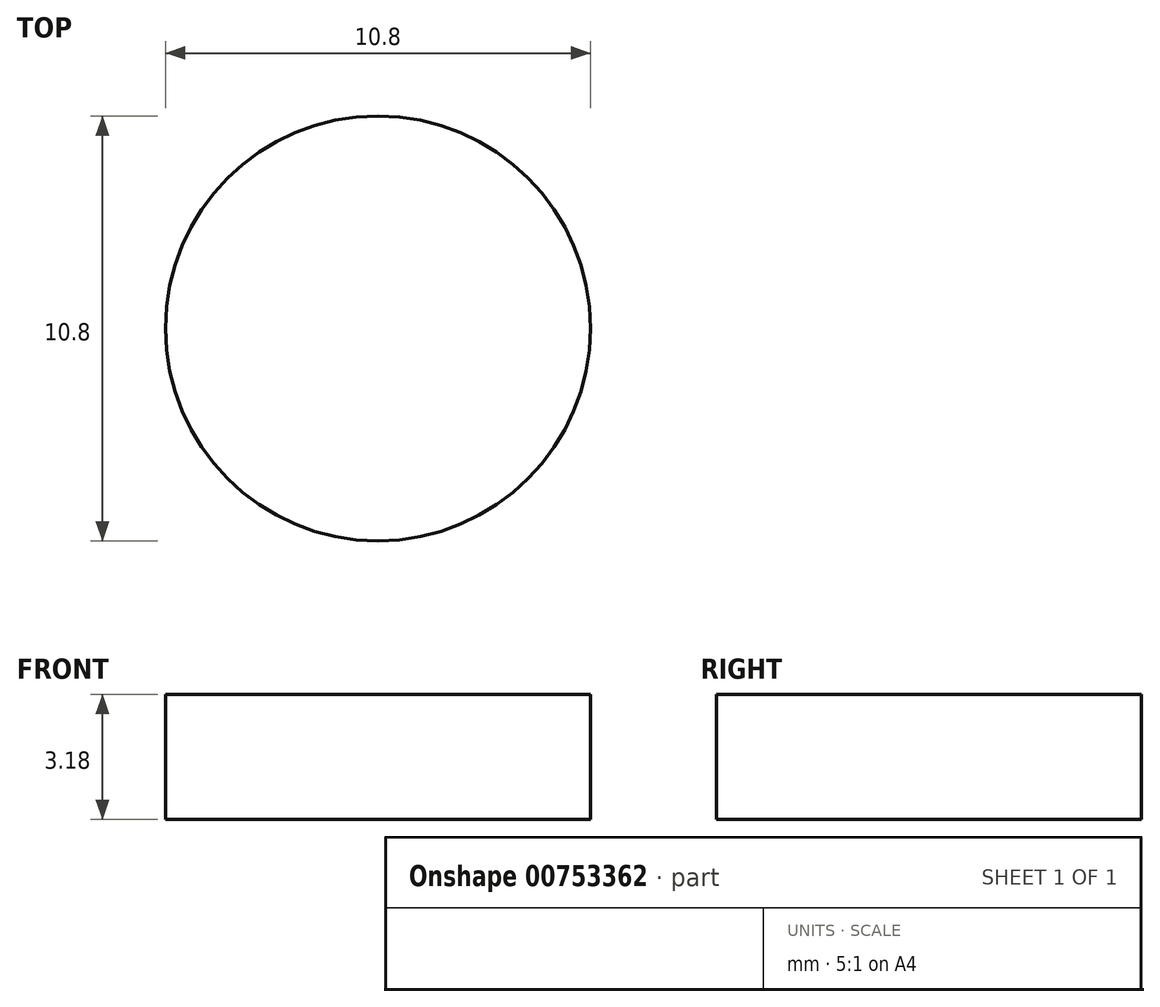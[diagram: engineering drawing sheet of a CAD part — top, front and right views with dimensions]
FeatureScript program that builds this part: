
annotation { "Feature Type Name" : "Feature", "Feature Type Description" : "" }
export const myFeature = defineFeature(function(context is Context, id is Id, definition is map)
    precondition{}
    {
        {
            var Q0;
            Q0=qCreatedBy(makeId("Top.planeOp"),FACE);
            var sketch = newSketch(context, id + "F0", { "sketchPlane" : qUnion([Q0])});
            skCircle(sketch, "E0", {"center": v(0, 0) * mm, "radius": 4.76 * mm, "construction": true});
            skCircle(sketch, "E1", {"center": v(0, 0) * mm, "radius": 5.4 * mm, "construction": true});
            skSolve(sketch);
        }
        {
            var Q0;
            Q0=qCreatedBy(makeId("Top.planeOp"),FACE);
            var sketch = newSketch(context, id + "F1", { "sketchPlane" : qUnion([Q0])});
            skCircle(sketch, "E2.0", {"center": v(0, 0) * mm, "radius": 5.4 * mm});
            skSolve(sketch);
        }
        {
            var Q0;
            Q0=sQuery(id+"F1.wireOp",EDGE,"E2.0");
            extrude(context, id + "F2", {"bodyType" : ToolBodyType.SURFACE, "surfaceEntities" : qUnion([Q0]), "depth" : 3.17 * mm, "offsetDistance" : 25.4 * mm});
        }
    });
